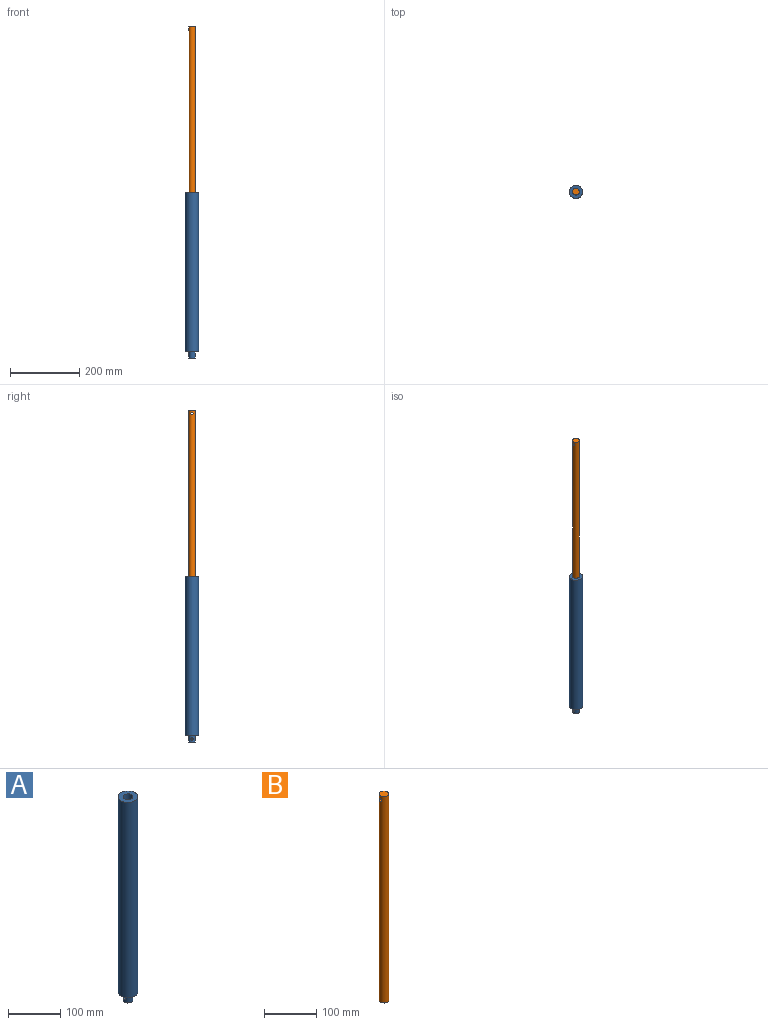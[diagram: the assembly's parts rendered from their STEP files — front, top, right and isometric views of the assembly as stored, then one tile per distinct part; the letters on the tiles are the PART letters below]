
ASSEMBLY  parts=2 mates=1
PART A: 8 faces, bbox 38.1x38.1x476.3 mm
  f0: cylinder r=9.53mm len=19.05mm, axis (0,0,1), area 1075.9mm2, adj f3,f6,f7
  f1: cylinder r=19.05mm len=457.2mm, axis (0,0,-1), area 54724.4mm2, adj f2,f3
  f2: plane 38.1x38.1mm, normal (0,0,1), area 855.1mm2, adj f1,f4
  f3: plane 38.1x38.1mm, normal (0,0,-1), area 855.1mm2, adj f0,f1
  f4: cylinder r=9.53mm len=447.68mm, axis (0,0,-1), area 26792.2mm2, adj f2,f5
  f5: plane 19.05x19.05mm, normal (0,0,1), area 285mm2, adj f4
  f6: plane 19.05x19.05mm, normal (0,0,-1), area 285mm2, adj f0
  f7: cylinder r=3.17mm len=19.05mm, axis (-1,0,0), area 369.2mm2, adj f0
PART B: 4 faces, bbox 19.1x19.1x482.6 mm
  f0: cylinder r=9.53mm len=482.6mm, axis (0,0,-1), area 28818.1mm2, adj f1,f2,f3
  f1: plane 19.05x19.05mm, normal (0,0,1), area 285mm2, adj f0
  f2: plane 19.05x19.05mm, normal (0,0,-1), area 285mm2, adj f0
  f3: cylinder r=3.17mm len=19.05mm, axis (1,0,0), area 369.2mm2, adj f0
PLACE A t=(-121.09,100.45,45.99)mm fixed
PLACE B t=(-121.09,100.45,284.11)mm
MATE slider A.f1 <-> B.f0  axis (0,0,1) through (-121.09,100.45,503.19)mm
